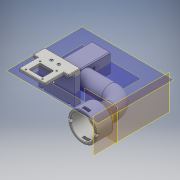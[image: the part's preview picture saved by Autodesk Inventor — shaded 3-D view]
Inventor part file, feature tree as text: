
AUTODESK INVENTOR PART (.ipt)
format: ipt  version: 2016 (Build 200138000, 138)  size: 580,608 bytes
history: native  units: mm
features: sketch x28, extrude x24, fillet x10, other x8, projected_geometry x3, loft x2, sweep x1
ambient origin geometry x8: Origin, YZ Plane, XZ Plane, XY Plane, X Axis, Y Axis, Z Axis, Center Point
bodies: Body1 (feature_tree)
feature tree (76):
  other  "ソリッド1"
  extrude  "押し出し1"  Depth=13.0mm TaperAngle=0.0deg
  fillet  "フィレット1"  Radius=1.0mm
  fillet  "フィレット2"  Radius=10.0mm
  sketch  "スケッチ2"
  extrude  "押し出し2"  Depth=10.0mm
  extrude  "押し出し3"  Depth=4.0mm TaperAngle=0.0deg
  sketch  "スケッチ3"
  extrude  "押し出し4"  Depth=4.0mm TaperAngle=0.0deg
  extrude  "押し出し5"  Depth=13.0mm
  extrude  "押し出し6"  Depth=13.0mm
  extrude  "押し出し7"  Depth=7.0mm TaperAngle=0.0deg
  fillet  "フィレット3"  Radius=7.0mm
  extrude  "押し出し8"  Depth=40.0mm
  extrude  "押し出し9"  Depth=40.0mm
  sketch  "スケッチ9"
  other  "作業平面1"
  sweep  "スイープ1"
  extrude  "押し出し10"  Depth=17.5mm
  sketch  "スケッチ12"
  other  "作業平面2"
  loft  "ロフト1"
  other  "作業平面3"
  loft  "ロフト2"
  extrude  "押し出し11"  Depth=25.0mm
  extrude  "押し出し12"  Depth=55.0mm TaperAngle=0.0deg
  fillet  "フィレット4"  Radius=20.0mm
  fillet  "フィレット5"  Radius=2.0mm
  other  "作業平面4"
  extrude  "押し出し13"  Depth=4.0mm
  other  "作業平面5"
  extrude  "押し出し14"  Depth=4.0mm
  extrude  "押し出し15"  Depth=4.0mm
  fillet  "フィレット6"  Radius=4.0mm
  fillet  "フィレット7"  Radius=2.0mm
  extrude  "押し出し20"  Depth=90.0mm TaperAngle=0.0deg
  extrude  "押し出し21"  Depth=4.0mm
  fillet  "フィレット8"  Radius=73.0mm
  fillet  "フィレット9"  Radius=14.0mm
  extrude  "押し出し22"  TaperAngle=90.0deg  [1 undecoded]
  extrude  "押し出し23"  TaperAngle=0.0deg  [1 undecoded]
  extrude  "押し出し24"  Depth=12.0mm TaperAngle=0.0deg
  extrude  "押し出し25"  Depth=12.0mm
  extrude  "押し出し26"  Depth=60.0mm
  extrude  "押し出し27"  TaperAngle=0.0deg  [1 undecoded]
  extrude  "押し出し28"  TaperAngle=0.0deg  [1 undecoded]
  fillet  "フィレット10"  [1 undecoded]
  sketch  "スケッチ1"
  sketch  "スケッチ4"
  sketch  "スケッチ5"
  sketch  "スケッチ6"
  sketch  "スケッチ7"
  sketch  "スケッチ10"
  sketch  "スケッチ11"
  projected_geometry  "投影ループ1"
  sketch  "スケッチ13"
  other  "エッジ1"
  sketch  "スケッチ15"
  sketch  "スケッチ18"
  sketch  "スケッチ19"
  sketch  "スケッチ20"
  projected_geometry  "投影ループ2"
  sketch  "スケッチ21"
  sketch  "スケッチ22"
  sketch  "スケッチ23"
  sketch  "スケッチ27"
  sketch  "スケッチ28"
  sketch  "スケッチ29"
  projected_geometry  "投影ループ3"
  sketch  "スケッチ30"
  sketch  "スケッチ31"
  sketch  "スケッチ32"
  sketch  "スケッチ33"
  sketch  "スケッチ34"
  sketch  "スケッチ35"
  other  "断面エッジを投影1"
note: 5 required parameter values undecoded (feature->parameter linkage not recoverable at this tier; creation-order binding heuristic only, values carry confidence <= 0.55)
